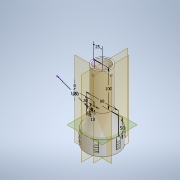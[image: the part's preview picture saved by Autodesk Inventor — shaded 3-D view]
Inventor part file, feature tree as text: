
AUTODESK INVENTOR PART (.ipt)
format: ipt  version: 2022.3 (Build 263350000, 350)  size: 460,288 bytes
history: native  units: mm
features: sketch x10, extrude x8, revolve x5, plane x4, hole x3, pattern_circular x2, mirror x2
ambient origin geometry x8: Origin, YZ Plane, XZ Plane, XY Plane, X Axis, Y Axis, Z Axis, Center Point
bodies: Solid1 (feature_tree)
feature tree (34):
  extrude  "Extrusion1"  Depth=4.0mm
  sketch  "Sketch2"  dims[d2=40.0mm d3=0.0mm d4=88.0mm]
  revolve  "Revolution1"  [1 undecoded]
  plane  "Work Plane1"
  extrude  "Extrusion2"  Depth=100.0mm
  sketch  "Sketch18"  dims[d5=50.0mm d8=100.0mm]
  extrude  "Extrusion11"  Depth=100.0mm
  extrude  "Extrusion12"  Depth=100.0mm
  extrude  "Extrusion13"  [1 undecoded]
  pattern_circular  "Circular Pattern2"  [2 undecoded]
  revolve  "Revolution4"  [1 undecoded]
  plane  "Work Plane3"
  plane  "Work Plane4"
  hole  "Hole5"  [1 undecoded]
  hole  "Hole6"  [1 undecoded]
  mirror  "Mirror1"
  mirror  "Mirror2"
  extrude  "Extrusion15"  Depth=50.0mm
  plane  "Work Plane5"
  sketch  "Sketch24"  dims[d16=75.0mm]
  revolve  "Revolution7"  [1 undecoded]
  hole  "Hole8"  [1 undecoded]
  pattern_circular  "Circular Pattern4"  [2 undecoded]
  extrude  "Extrusion16"  Depth=50.0mm TaperAngle=0.0deg
  extrude  "Extrusion17"  Depth=50.0mm
  revolve  "Revolution15"  [1 undecoded]
  revolve  "Revolution16"  [1 undecoded]
  sketch  "Sketch1"  dims[d0=80.0mm d1=4.0mm]
  sketch  "Sketch19"  dims[d9=25.0mm d10=100.0mm]
  sketch  "Sketch20"  dims[d11=4.0mm d12=100.0mm]
  sketch  "Sketch21"  dims[d13=360.0deg d14=-45.0mm]
  sketch  "Sketch22"  dims[d15=5.0mm]
  sketch  "Sketch25"  dims[d17=75.0mm]
  sketch  "Sketch26"  dims[d18=5.0mm d19=15.0mm d20=5.2mm d21=5.0mm d22=0.0mm d79=0.0mm d106=4.0mm d107=10.0mm d108=30.0mm d109=0.0mm d110=10.0mm d111=30.0mm d112=0.0mm d113=1.0mm d114=10.0mm d115=1.0mm d116=3.0mm d117=1.0mm d118=5.0mm d119=1.0mm d120=4.0mm d121=1.0mm d122=5.0mm d123=10.0mm d124=90.0deg d131=10.0mm d132=0.0mm d133=1.0mm d134=3.0mm d135=60.0mm d136=360.0deg d138=2.0mm d139=5.0mm d140=2.0mm d141=5.0mm d142=90.0deg d143=25.0mm d144=25.0mm d145=30.0mm d146=3.4mm d147=6.0mm d148=5.9mm d149=2.0mm d150=90.0deg d151=4.2mm d152=0.0mm d153=30.0mm d154=180.0deg d155=3.4mm d156=6.0mm d157=5.9mm d158=2.0mm d159=90.0deg d160=4.2mm d161=0.0mm d165=4.0mm d166=10.0mm d167=0.0mm d168=6.6mm d181=10.0mm d182=10.0mm d183=90.0deg d184=5.0mm d185=2.0mm d186=2.2mm d187=6.0mm d188=3.1mm d189=4.1mm d190=90.0deg d191=0.9mm d192=0.0mm d193=20.0mm d194=90.0deg d196=20.0mm d197=20.0mm d198=15.0mm d199=10.0mm d202=10.0mm d203=10.0mm d204=10.0mm d205=1.0mm d206=5.0mm d207=2.0mm d208=5.0mm d209=1.0mm d215=120.0mm d216=0.0mm d217=50.0mm d218=0.0mm d219=300.0deg d220=360.0deg d125=0.872665mm d126=0.872665mm d137=14.3117mm d164=2.25mm d212=0.872665mm d213=0.872665mm]
note: 13 required parameter values undecoded (feature->parameter linkage not recoverable at this tier; creation-order binding heuristic only, values carry confidence <= 0.55)